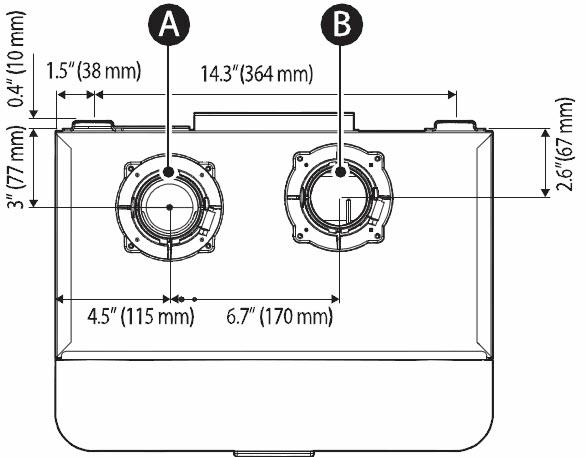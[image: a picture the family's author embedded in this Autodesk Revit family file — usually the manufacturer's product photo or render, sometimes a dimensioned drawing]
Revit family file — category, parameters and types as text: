
# Revit family: Water_Heater-Racks-Navien-NPE-11_Unit_Back_to_Back---
name_source: partatom
category: Mechanical Equipment
revit_build: Autodesk Revit 2016 (Build: 20150220_1215(x64)
units: mm (PartAtom-declared; Revit-internal decimal feet)

## family parameters
Cut with Voids When Loaded = No
Host = Face
OmniClass Number = 23.65.35.11
OmniClass Title = Supply Water Heaters
Part Type = Normal
Room Calculation Point = No
Round Connector Dimension = Use Diameter
Shared = No

## types (4) — shared parameters
2" Exhaust/Intake = Yes
3" Exhaust/Intake = No
Apparent Load = 0 VA
Assembly Code = D3010500
Certifications = Energy Star | AHRI | CSA | CSA | NFS
Cold Water Inlet = 1"
Configuration = NPE_B11_4B4B_3B
Default Elevation = 48 "
Depth = 23.8 "
Description = 11 Unit Back to Back
Exhaust = 2"
Finish = Metal - Navien - White
Flow Rate = 1 GPM
Flow Rate Note = 35°F (19°C) temp rise: 11.2 GPM (42 L/m) | 45°F (25°C) temp rise: 8.7 GPM (33 L/m) | 67°F (36°C) temp rise: NPE-240A: 5.6 GPM(21 L/m), NPE-240S: 5.7 GPM(22 L/m)
Frequency = 60 Hz
Gas Inlet = 1"
Heating Capacity = 120000.0 Btu/h
Heating Capacity Note = 19,900–199,900 (BTU/H)
Height = 65.5 "
Hot Water Outlet = 1"
Ignition = Electronic ignition
Installation Type = Indoor
Intake = 2"
Keynote = 22 33 00.A1
Manifold(s) = (3) 30019042A
Manufacturer = Navien, Inc.
Manufacturer Fax Number = (949) 420-0430
Natural Gas Manifold Pressure = -0.05" WC to -0.58" WC
Natural Gas Supply Pressure = 3.5"–10.5" WC
Number of Poles = 1
Phase = 1
Power Factor = 1
Product Documentation Link = https://www.navieninc.com
Product Name = NPE Series Tankless Water Heaters w/ Racks
Product Page URL = https://www.navieninc.com
Propane Gas Manifold Pressure = -0.10" WC to -0.78" WC
Propane Gas Supply Pressure = 8"–13" WC
Rack(s) = (2) GFFM-KDIZUS-003 + (4) GFFM-KDIZUS-004
Required Cascade Operation Accessory = (11) 30014367A (Common Vent Damper & Cascade Communication Cable) or (10) GXXX000546 (Individual Vent Cascade Communication Cable)
URL = https://www.navieninc.com
Venting = Exhaust: 2" PVC, CPVC, PP, SS / 2" special gas vent type BH (Class II, A/B/C) | Intake: 2" PVC, CPVC, PP, SS / 2" special gas vent type BH (Class II, A/B/C) | Vent clearances: 0" to combustibles
Venting Type = Forced draft direct vent
Version = 2016 - v1.0.a
Voltage = 120 V
Water Pressure = 15–150 PSI
Wi-Fi Ready = NaviLink Wi-Fi Control: PBCM-AS-001
Width = 142.3 "

## per-type parameters (varying)
| type | Constraints | Model | Natural Gas | Propane Gas | Recirculation Inlet | Recirculation Inlet Visibility | Tankless Water Heaters | Weight |
| Natural Gas - Recirculating System - NPE-240A(Advanced)-NG | 6 | (11) NPE-240A-NG | Yes | No | 0" | Yes | (11) NPE-240A-NG | 82.00 lbf |
| Natural Gas - NPE-240S(Standard)-NG | 7 | (11) NPE-240S-NG | Yes | No | 1" | No | (11) NPE-240S-NG | 75.00 lbf |
| Propane Gas - Recirculating System - NPE-240A(Advanced)-LPG | 6 | (11) NPE-240A-LPG | No | Yes | 0" | Yes | (11) NPE-240A-LPG | 82.00 lbf |
| Propane Gas - NPE-240S(Standard)-LPG | 7 | (11) NPE-240S-LPG | No | Yes | 1" | No | (11) NPE-240S-LPG | 75.00 lbf |

## geometry (parser evidence)
native form markers: Sweep x16
no freeform markers — native parametric forms only
